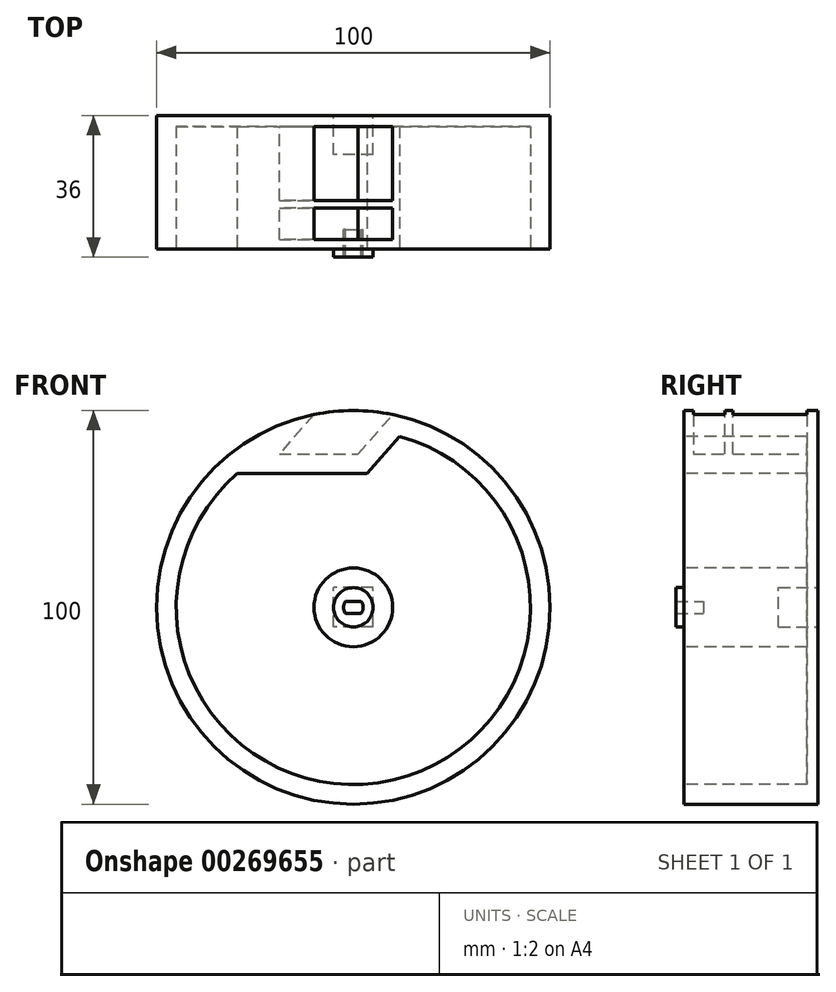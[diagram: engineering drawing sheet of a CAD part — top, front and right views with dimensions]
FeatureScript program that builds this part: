
annotation { "Feature Type Name" : "Feature", "Feature Type Description" : "" }
export const myFeature = defineFeature(function(context is Context, id is Id, definition is map)
    precondition{}
    {
        {
            var Q0;
            Q0=qCreatedBy(makeId("Front.planeOp"),FACE);
            var sketch = newSketch(context, id + "F0", { "sketchPlane" : qUnion([Q0])});
            skArc(sketch, "E0", {"start": v(-10, 48.99) * mm, "mid": v(0, -50) * mm, "end": v(10, 48.99) * mm});
            skLineSegment(sketch, "E1", {"start": v(-10, 48.99) * mm, "end": v(10, 48.99) * mm, "construction": true});
            skLineSegment(sketch, "E2", {"start": v(0, 0) * mm, "end": v(0, 48.99) * mm, "construction": true});
            skPoint(sketch, "E2.endSnap0", {"position": v(0, 9.17) * mm});
            skLineSegment(sketch, "E3", {"start": v(1.23, 38.99) * mm, "end": v(10, 48.99) * mm});
            skLineSegment(sketch, "E4", {"start": v(-10, 48.99) * mm, "end": v(-18.77, 38.99) * mm});
            skLineSegment(sketch, "E5", {"start": v(-18.77, 38.99) * mm, "end": v(1.23, 38.99) * mm});
            skSolve(sketch);
        }
        {
            var Q0;
            Q0=makeQuery(id+"F0.imprint","IMPRINT",FACE,{"disambiguationData":[TD([[makeQuery(id+"F0.imprint","IMPRINT",EDGE,{"derivedFrom":sQuery(id+"F0.wireOp",EDGE,"E0")}),1.0]])]});
            extrude(context, id + "F1", {"entities" : qUnion([Q0]), "depth" : 34 * mm});
        }
        {
            var Q0;
            Q0=makeQuery(id+"F1.opExtrude","CAP_FACE",FACE,{"disambiguationData":[OSD([sQuery(id+"F0.wireOp",EDGE,"E0"),sQuery(id+"F0.wireOp",EDGE,"8V0HQv4A-RKj5-sdPm-ng19-TvgYM00hYBG8"),sQuery(id+"F0.wireOp",EDGE,"PA5xsDWG-WYoZ-letV-uS6d-CdA2JmXPh8sm"),sQuery(id+"F0.wireOp",EDGE,"E3")])],"isStart":false});
            var sketch = newSketch(context, id + "F2", { "sketchPlane" : qUnion([Q0])});
            skArc(sketch, "E6.0", {"start": v(-13.64, 48.1) * mm, "mid": v(0, -50) * mm, "end": v(13.64, 48.1) * mm});
            skArc(sketch, "E7", {"start": v(13.64, 48.1) * mm, "mid": v(0, 50) * mm, "end": v(-13.64, 48.1) * mm});
            skSolve(sketch);
        }
        {
            var Q0;
            Q0 = qSketchRegion(id + "F2", true);
            extrude(context, id + "F3", {"entities" : qUnion([Q0]), "operationType" : NewBodyOperationType.ADD, "oppositeDirection" : true, "depth" : 2.4 * mm});
        }
        {
            var Q0;
            Q0=makeQuery(id+"F1.opExtrude","CAP_FACE",FACE,{"disambiguationData":[OSD([sQuery(id+"F0.wireOp",EDGE,"E0"),sQuery(id+"F0.wireOp",EDGE,"8V0HQv4A-RKj5-sdPm-ng19-TvgYM00hYBG8"),sQuery(id+"F0.wireOp",EDGE,"PA5xsDWG-WYoZ-letV-uS6d-CdA2JmXPh8sm"),sQuery(id+"F0.wireOp",EDGE,"E3")])],"isStart":true});
            var sketch = newSketch(context, id + "F4", { "sketchPlane" : qUnion([Q0])});
            skArc(sketch, "E8.0", {"start": v(-13.64, 48.1) * mm, "mid": v(0, -50) * mm, "end": v(13.64, 48.1) * mm});
            skArc(sketch, "E9", {"start": v(13.64, 48.1) * mm, "mid": v(0, 50) * mm, "end": v(-13.64, 48.1) * mm});
            skSolve(sketch);
        }
        {
            var Q0;
            Q0 = qSketchRegion(id + "F4", true);
            extrude(context, id + "F5", {"entities" : qUnion([Q0]), "operationType" : NewBodyOperationType.ADD, "oppositeDirection" : true, "depth" : 2.8 * mm});
        }
        {
            var Q0;
            Q0=makeQuery(id+"F3.boolean.opBoolean","MERGE",FACE,{"derivedFrom":[makeQuery(id+"F1.opExtrude","CAP_FACE",FACE,{"disambiguationData":[OSD([sQuery(id+"F0.wireOp",EDGE,"E0"),sQuery(id+"F0.wireOp",EDGE,"8V0HQv4A-RKj5-sdPm-ng19-TvgYM00hYBG8"),sQuery(id+"F0.wireOp",EDGE,"PA5xsDWG-WYoZ-letV-uS6d-CdA2JmXPh8sm"),sQuery(id+"F0.wireOp",EDGE,"E3")])],"isStart":false}),makeQuery(id+"F3.opExtrude","CAP_FACE",FACE,{"disambiguationData":[OSD([sQuery(id+"F2.wireOp",EDGE,"E6.0"),sQuery(id+"F2.wireOp",EDGE,"E7")])],"isStart":true})]});
            cPlane(context, id + "F6", {"entities" : qUnion([Q0]), "cplaneType" : CPlaneType.OFFSET, "offset" : 10.4 * mm, "oppositeDirection" : true, "width" : 150 * mm, "height" : 150 * mm});
        }
        {
            var Q0;
            Q0=qCreatedBy(id+"F6.planeOp",FACE);
            var sketch = newSketch(context, id + "F7", { "sketchPlane" : qUnion([Q0])});
            skArc(sketch, "E10.0", {"start": v(-13.64, 48.1) * mm, "mid": v(0, -50) * mm, "end": v(13.64, 48.1) * mm});
            skArc(sketch, "E11", {"start": v(13.64, 48.1) * mm, "mid": v(0, 50) * mm, "end": v(-13.64, 48.1) * mm});
            skSolve(sketch);
        }
        {
            var Q0;
            Q0 = qSketchRegion(id + "F7", true);
            extrude(context, id + "F8", {"entities" : qUnion([Q0]), "operationType" : NewBodyOperationType.ADD, "oppositeDirection" : true, "depth" : 2 * mm});
        }
        {
            var Q0;
            Q0=makeQuery(id+"F5.boolean.opBoolean","MERGE",FACE,{"derivedFrom":[makeQuery(id+"F1.opExtrude","CAP_FACE",FACE,{"disambiguationData":[OSD([sQuery(id+"F0.wireOp",EDGE,"E0"),sQuery(id+"F0.wireOp",EDGE,"8V0HQv4A-RKj5-sdPm-ng19-TvgYM00hYBG8"),sQuery(id+"F0.wireOp",EDGE,"PA5xsDWG-WYoZ-letV-uS6d-CdA2JmXPh8sm"),sQuery(id+"F0.wireOp",EDGE,"E3")])],"isStart":true}),makeQuery(id+"F5.opExtrude","CAP_FACE",FACE,{"disambiguationData":[OSD([sQuery(id+"F4.wireOp",EDGE,"E8.0"),sQuery(id+"F4.wireOp",EDGE,"E9")])],"isStart":true})]});
            var sketch = newSketch(context, id + "F9", { "sketchPlane" : qUnion([Q0])});
            skCircle(sketch, "E12", {"center": v(0, 0) * mm, "radius": 5 * mm, "construction": true});
            skLineSegment(sketch, "E13", {"start": v(0, -11.26) * mm, "end": v(0, 12.45) * mm, "construction": true});
            skLineSegment(sketch, "E14", {"start": v(17.58, 0) * mm, "end": v(-15.35, 0) * mm, "construction": true});
            skLineSegment(sketch, "E15.bottom", {"start": v(-5, -5) * mm, "end": v(5, -5) * mm});
            skLineSegment(sketch, "E15.top", {"start": v(-5, 5) * mm, "end": v(5, 5) * mm});
            skLineSegment(sketch, "E15.left", {"start": v(-5, -5) * mm, "end": v(-5, 5) * mm});
            skLineSegment(sketch, "E15.right", {"start": v(5, -5) * mm, "end": v(5, 5) * mm});
            skSolve(sketch);
        }
        {
            var Q0;
            Q0 = qSketchRegion(id + "F9", true);
            extrude(context, id + "F10", {"entities" : qUnion([Q0]), "operationType" : NewBodyOperationType.REMOVE, "oppositeDirection" : true, "depth" : 10 * mm});
        }
        {
            var Q0;
            Q0=makeQuery(id+"F3.boolean.opBoolean","MERGE",FACE,{"derivedFrom":[makeQuery(id+"F1.opExtrude","CAP_FACE",FACE,{"disambiguationData":[OSD([sQuery(id+"F0.wireOp",EDGE,"E0"),sQuery(id+"F0.wireOp",EDGE,"8V0HQv4A-RKj5-sdPm-ng19-TvgYM00hYBG8"),sQuery(id+"F0.wireOp",EDGE,"PA5xsDWG-WYoZ-letV-uS6d-CdA2JmXPh8sm"),sQuery(id+"F0.wireOp",EDGE,"E3")])],"isStart":false}),makeQuery(id+"F3.opExtrude","CAP_FACE",FACE,{"disambiguationData":[OSD([sQuery(id+"F2.wireOp",EDGE,"E6.0"),sQuery(id+"F2.wireOp",EDGE,"E7")])],"isStart":true})]});
            var sketch = newSketch(context, id + "F11", { "sketchPlane" : qUnion([Q0])});
            skCircle(sketch, "E16", {"center": v(0, 0) * mm, "radius": 5 * mm});
            skLineSegment(sketch, "E17", {"start": v(-1, 0) * mm, "end": v(1, 0) * mm, "construction": true});
            skLineSegment(sketch, "E18", {"start": v(0, -5) * mm, "end": v(0, 5) * mm, "construction": true});
            skPoint(sketch, "E19.orphan", {"position": v(0, -1.93) * mm});
            skArc(sketch, "E20", {"start": v(-1.96, 1.55) * mm, "mid": v(-2.5, 0) * mm, "end": v(-1.96, -1.55) * mm});
            skLineSegment(sketch, "E21", {"start": v(-1.96, 1.55) * mm, "end": v(1.96, 1.55) * mm});
            skLineSegment(sketch, "E22", {"start": v(1.96, -1.55) * mm, "end": v(-1.96, -1.55) * mm});
            skArc(sketch, "E23.trimOffspring", {"start": v(1.96, -1.55) * mm, "mid": v(2.5, 0) * mm, "end": v(1.96, 1.55) * mm});
            skSolve(sketch);
        }
        {
            var Q0;
            Q0 = qSketchRegion(id + "F11", true);
            extrude(context, id + "F12", {"entities" : qUnion([Q0]), "operationType" : NewBodyOperationType.ADD, "depth" : 2 * mm});
        }
        {
            var Q0;
            Q0=makeQuery(id+"F12.boolean.opBoolean","SPLIT",FACE,{"disambiguationData":[TD([makeQuery(id+"F12.opExtrude","SWEPT_FACE",FACE,{"disambiguationData":[OSD([sQuery(id+"F11.wireOp",EDGE,"E20")])]})])],"derivedFrom":makeQuery(id+"F3.boolean.opBoolean","MERGE",FACE,{"derivedFrom":[makeQuery(id+"F1.opExtrude","CAP_FACE",FACE,{"disambiguationData":[OSD([sQuery(id+"F0.wireOp",EDGE,"E0"),sQuery(id+"F0.wireOp",EDGE,"8V0HQv4A-RKj5-sdPm-ng19-TvgYM00hYBG8"),sQuery(id+"F0.wireOp",EDGE,"PA5xsDWG-WYoZ-letV-uS6d-CdA2JmXPh8sm"),sQuery(id+"F0.wireOp",EDGE,"E3")])],"isStart":false}),makeQuery(id+"F3.opExtrude","CAP_FACE",FACE,{"disambiguationData":[OSD([sQuery(id+"F2.wireOp",EDGE,"E6.0"),sQuery(id+"F2.wireOp",EDGE,"E7")])],"isStart":true})]})});
            extrude(context, id + "F13", {"entities" : qUnion([Q0]), "operationType" : NewBodyOperationType.REMOVE, "oppositeDirection" : true, "depth" : 5 * mm});
        }
        {
            var Q0;
            {var subQ0=sQuery(id+"F2.wireOp",EDGE,"E7");var subQ1=sQuery(id+"F2.wireOp",EDGE,"E6.0");var subQ2=sQuery(id+"F0.wireOp",EDGE,"E0");Q0=makeQuery(id+"F12.boolean.opBoolean","SPLIT",FACE,{"disambiguationData":[TD([makeQuery(id+"F1.opExtrude","SWEPT_FACE",FACE,{"disambiguationData":[OSD([subQ2])]})])],"derivedFrom":makeQuery(id+"F3.boolean.opBoolean","MERGE",FACE,{"derivedFrom":[makeQuery(id+"F1.opExtrude","CAP_FACE",FACE,{"disambiguationData":[OSD([subQ2,sQuery(id+"F0.wireOp",EDGE,"PA5xsDWG-WYoZ-letV-uS6d-CdA2JmXPh8sm"),sQuery(id+"F0.wireOp",EDGE,"E3"),sQuery(id+"F0.wireOp",EDGE,"bI9qW1cQ-SzVL-Mkbr-Relv-HGwP7shOylkU")])],"isStart":false}),makeQuery(id+"F3.opExtrude","CAP_FACE",FACE,{"disambiguationData":[OSD([subQ1,subQ0])],"isStart":true})]})});}
            var sketch = newSketch(context, id + "F14", { "sketchPlane" : qUnion([Q0])});
            skArc(sketch, "E24.0", {"start": v(-29.5, 33.99) * mm, "mid": v(10.04, -43.87) * mm, "end": v(11.78, 43.43) * mm});
            skLineSegment(sketch, "E25.2", {"start": v(3.5, 33.99) * mm, "end": v(11.78, 43.43) * mm});
            skCircle(sketch, "E26.0", {"center": v(0, 0) * mm, "radius": 10 * mm});
            skLineSegment(sketch, "E27.0", {"start": v(-29.5, 33.99) * mm, "end": v(3.5, 33.99) * mm});
            skSolve(sketch);
        }
        {
            var Q0;
            Q0 = qSketchRegion(id + "F14", true);
            var Q1;
            Q1=makeQuery(id+"F5.boolean.opBoolean","INTERSECT",VERTEX,{"derivedFrom":[makeQuery(id+"F1.opExtrude","SWEPT_FACE",FACE,{"disambiguationData":[OSD([sQuery(id+"F0.wireOp",EDGE,"E3")])]}),makeQuery(id+"F1.opExtrude","SWEPT_FACE",FACE,{"disambiguationData":[OSD([sQuery(id+"F0.wireOp",EDGE,"bI9qW1cQ-SzVL-Mkbr-Relv-HGwP7shOylkU")])]}),makeQuery(id+"F5.opExtrude","CAP_FACE",FACE,{"disambiguationData":[OSD([sQuery(id+"F4.wireOp",EDGE,"E8.0"),sQuery(id+"F4.wireOp",EDGE,"E9")])],"isStart":false})]});
            extrude(context, id + "F15", {"entities" : qUnion([Q0]), "operationType" : NewBodyOperationType.REMOVE, "endBound" : BoundingType.UP_TO_VERTEX, "oppositeDirection" : true, "endBoundEntityVertex" : qUnion([Q1]), "depth" : 25 * mm});
        }
    });
